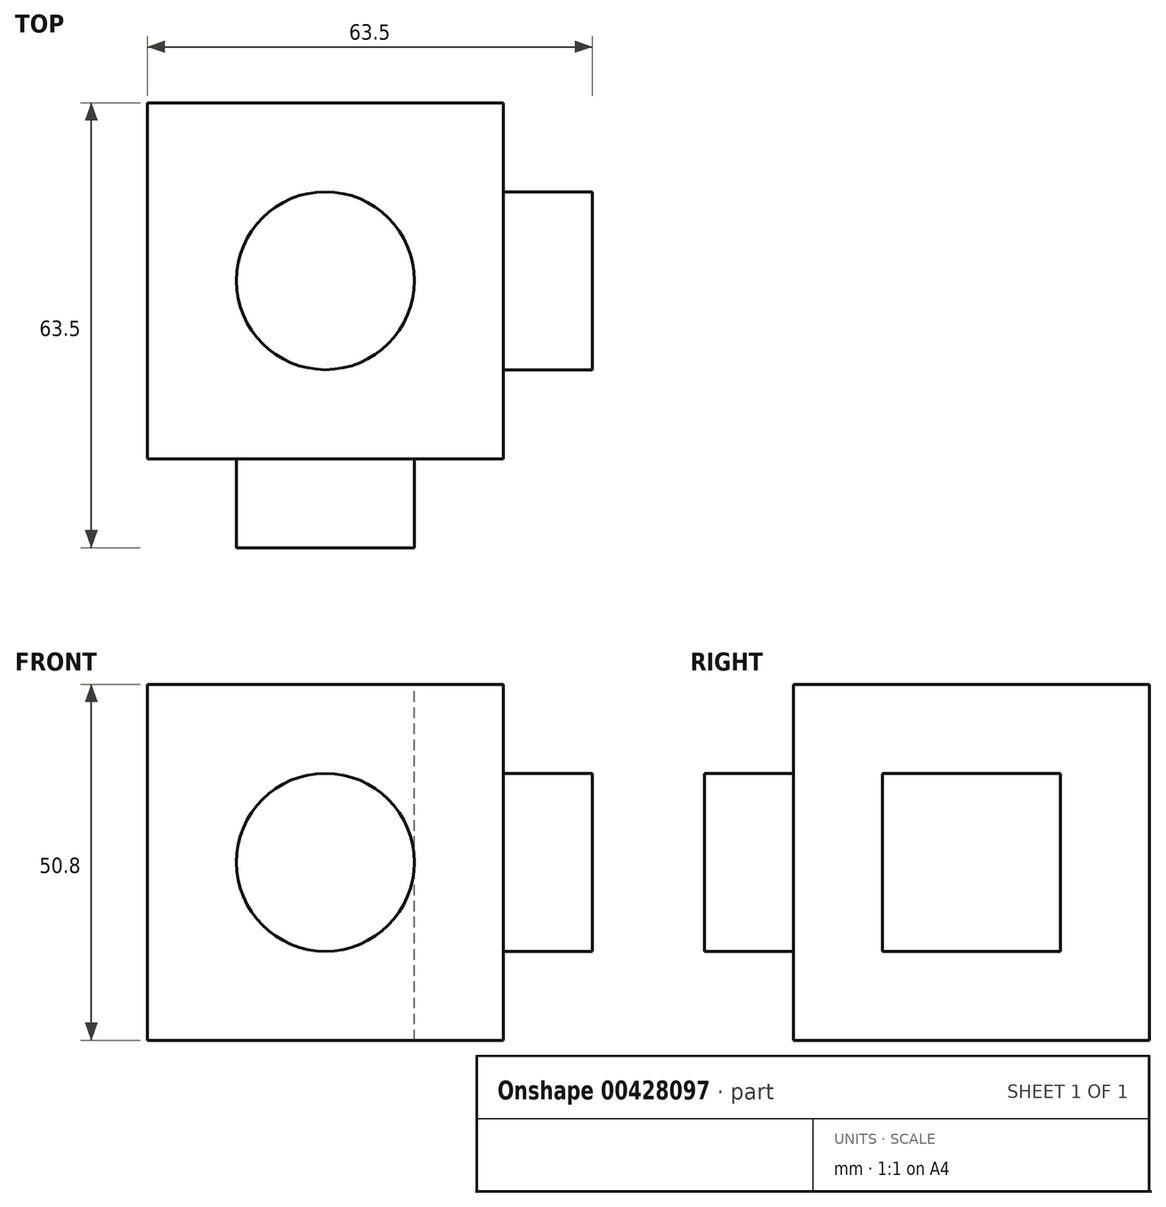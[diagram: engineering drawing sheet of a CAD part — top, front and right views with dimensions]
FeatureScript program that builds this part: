
annotation { "Feature Type Name" : "Feature", "Feature Type Description" : "" }
export const myFeature = defineFeature(function(context is Context, id is Id, definition is map)
    precondition{}
    {
        {
            var Q0;
            Q0=qCreatedBy(makeId("Front.planeOp"),FACE);
            var sketch = newSketch(context, id + "F0", { "sketchPlane" : qUnion([Q0])});
            skLineSegment(sketch, "E0", {"start": v(0, 0) * mm, "end": v(-50.8, 0) * mm});
            skLineSegment(sketch, "E1", {"start": v(-50.8, 0) * mm, "end": v(-50.8, 50.8) * mm});
            skLineSegment(sketch, "E2", {"start": v(-50.8, 50.8) * mm, "end": v(0, 50.8) * mm});
            skLineSegment(sketch, "E3", {"start": v(0, 50.8) * mm, "end": v(0, 0) * mm});
            skSolve(sketch);
        }
        {
            var Q0;
            Q0 = qSketchRegion(id + "F0", true);
            extrude(context, id + "F1", {"entities" : qUnion([Q0]), "depth" : 50.8 * mm});
        }
        {
            var Q0;
            Q0=makeQuery(id+"F1.opExtrude","SWEPT_FACE",FACE,{"disambiguationData":[OSD([sQuery(id+"F0.wireOp",EDGE,"E3")])]});
            var sketch = newSketch(context, id + "F2", { "sketchPlane" : qUnion([Q0])});
            skLineSegment(sketch, "E4.bottom", {"start": v(-38.1, 38.1) * mm, "end": v(-12.7, 38.1) * mm});
            skLineSegment(sketch, "E4.top", {"start": v(-38.1, 12.7) * mm, "end": v(-12.7, 12.7) * mm});
            skLineSegment(sketch, "E4.left", {"start": v(-38.1, 38.1) * mm, "end": v(-38.1, 12.7) * mm});
            skLineSegment(sketch, "E4.right", {"start": v(-12.7, 38.1) * mm, "end": v(-12.7, 12.7) * mm});
            skSolve(sketch);
        }
        {
            var Q0;
            Q0=makeQuery(id+"F2.imprint","IMPRINT",FACE,{"disambiguationData":[TD([[makeQuery(id+"F2.imprint","IMPRINT",EDGE,{"derivedFrom":sQuery(id+"F2.wireOp",EDGE,"E4.bottom")}),-1.0]])]});
            extrude(context, id + "F3", {"entities" : qUnion([Q0]), "operationType" : NewBodyOperationType.ADD, "depth" : 12.7 * mm});
        }
        {
            var Q0;
            Q0=makeQuery(id+"F1.opExtrude","CAP_FACE",FACE,{"disambiguationData":[OSD([sQuery(id+"F0.wireOp",EDGE,"E0"),sQuery(id+"F0.wireOp",EDGE,"E1"),sQuery(id+"F0.wireOp",EDGE,"E2"),sQuery(id+"F0.wireOp",EDGE,"E3")])],"isStart":false});
            var sketch = newSketch(context, id + "F4", { "sketchPlane" : qUnion([Q0])});
            skCircle(sketch, "E5", {"center": v(-25.4, 25.4) * mm, "radius": 12.7 * mm});
            skPoint(sketch, "E5.centerSnap0", {"position": v(0, 25.4) * mm});
            skPoint(sketch, "E5.centerSnap1", {"position": v(-25.4, 50.8) * mm});
            skSolve(sketch);
        }
        {
            var Q0;
            Q0 = qSketchRegion(id + "F4", true);
            extrude(context, id + "F5", {"entities" : qUnion([Q0]), "operationType" : NewBodyOperationType.ADD, "depth" : 12.7 * mm});
        }
        {
            var Q0;
            Q0=makeQuery(id+"F1.opExtrude","SWEPT_FACE",FACE,{"disambiguationData":[OSD([sQuery(id+"F0.wireOp",EDGE,"E2")])]});
            var sketch = newSketch(context, id + "F6", { "sketchPlane" : qUnion([Q0])});
            skCircle(sketch, "E6", {"center": v(-25.4, -25.4) * mm, "radius": 12.7 * mm});
            skPoint(sketch, "E6.centerSnap0", {"position": v(0, -25.4) * mm});
            skPoint(sketch, "E6.centerSnap1", {"position": v(-25.4, 0) * mm});
            skSolve(sketch);
        }
        {
            var Q0;
            Q0 = qSketchRegion(id + "F6", true);
            extrude(context, id + "F7", {"entities" : qUnion([Q0]), "operationType" : NewBodyOperationType.REMOVE, "oppositeDirection" : true, "depth" : 50.8 * mm});
        }
    });
